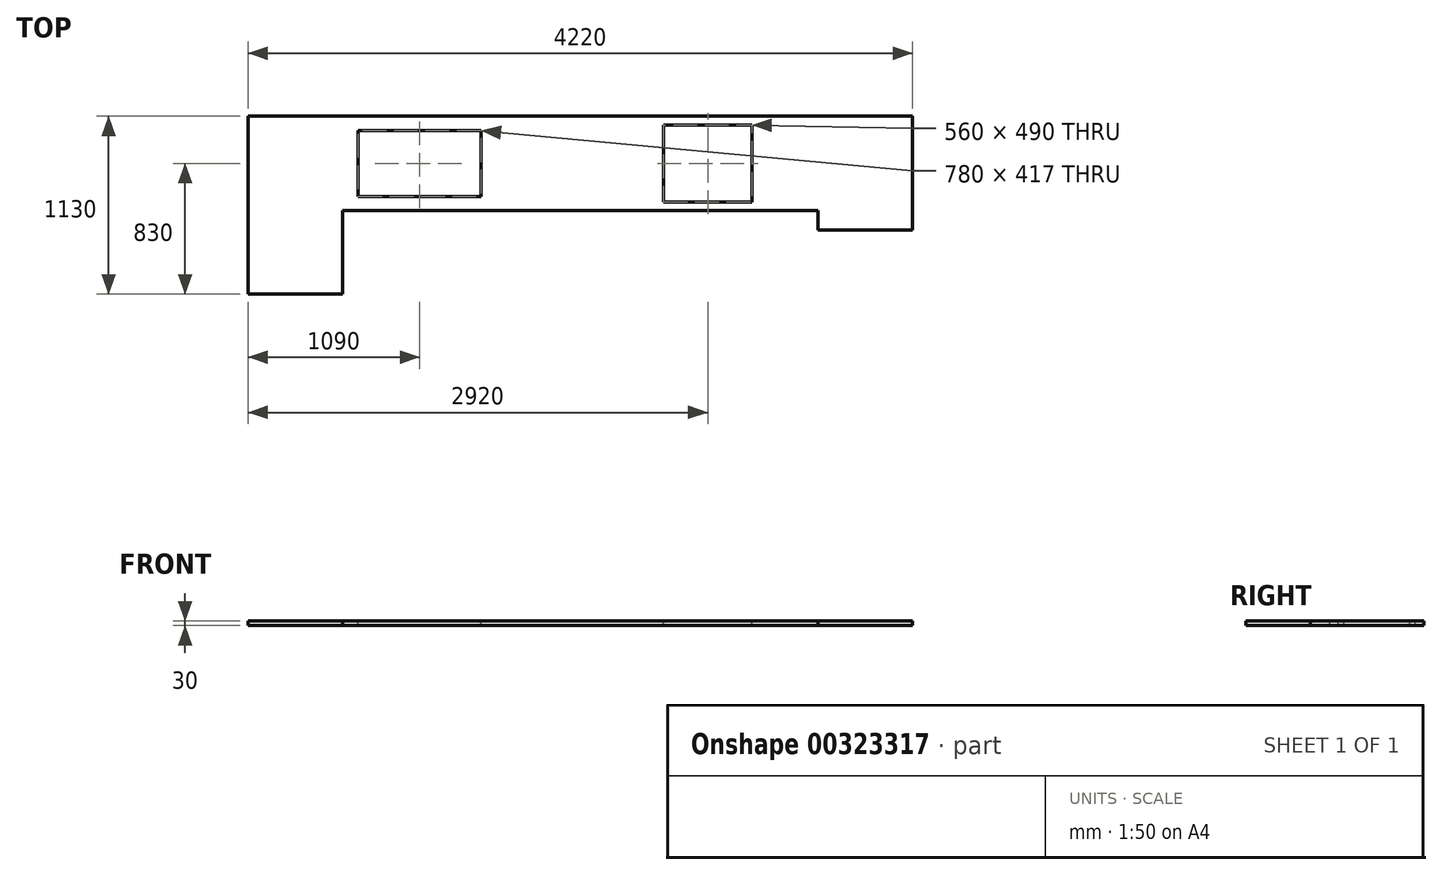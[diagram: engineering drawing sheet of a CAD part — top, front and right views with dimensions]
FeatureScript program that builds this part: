
annotation { "Feature Type Name" : "Feature", "Feature Type Description" : "" }
export const myFeature = defineFeature(function(context is Context, id is Id, definition is map)
    precondition{}
    {
        {
            var Q0;
            Q0=qCreatedBy(makeId("Top.planeOp"),FACE);
            var sketch = newSketch(context, id + "F0", { "sketchPlane" : qUnion([Q0])});
            skLineSegment(sketch, "E0", {"start": v(0, 0) * mm, "end": v(0, 1760) * mm});
            skLineSegment(sketch, "E1", {"start": v(0, 1760) * mm, "end": v(4220, 1760) * mm});
            skLineSegment(sketch, "E2", {"start": v(4220, 1760) * mm, "end": v(4220, 0) * mm});
            skLineSegment(sketch, "E3.0", {"start": v(600, 1160) * mm, "end": v(3620, 1160) * mm});
            skLineSegment(sketch, "E4.0", {"start": v(600, 0) * mm, "end": v(600, 1160) * mm});
            skLineSegment(sketch, "E5.0", {"start": v(3620, 1160) * mm, "end": v(3620, 0) * mm});
            skLineSegment(sketch, "E6", {"start": v(600, 0) * mm, "end": v(0, 0) * mm});
            skLineSegment(sketch, "E7", {"start": v(3620, 0) * mm, "end": v(4220, 0) * mm});
            skSolve(sketch);
        }
        {
            var Q0;
            Q0=qSketchRegion(id+"F0",true);
            extrude(context, id + "F1", {"entities" : qUnion([Q0]), "depth" : 30 * mm});
        }
        {
            var Q0;
            Q0=makeQuery(id+"F1.opExtrude","CAP_FACE",FACE,{"disambiguationData":[OSD([sQuery(id+"F0.wireOp",EDGE,"E0"),sQuery(id+"F0.wireOp",EDGE,"E1"),sQuery(id+"F0.wireOp",EDGE,"E2"),sQuery(id+"F0.wireOp",EDGE,"E3.0"),sQuery(id+"F0.wireOp",EDGE,"E4.0"),sQuery(id+"F0.wireOp",EDGE,"E5.0"),sQuery(id+"F0.wireOp",EDGE,"E6"),sQuery(id+"F0.wireOp",EDGE,"E7")])],"isStart":false});
            var sketch = newSketch(context, id + "F2", { "sketchPlane" : qUnion([Q0])});
            skLineSegment(sketch, "E8.bottom", {"start": v(700, 1251.5) * mm, "end": v(1480, 1251.5) * mm});
            skLineSegment(sketch, "E8.top", {"start": v(700, 1668.5) * mm, "end": v(1480, 1668.5) * mm});
            skLineSegment(sketch, "E8.left", {"start": v(700, 1251.5) * mm, "end": v(700, 1668.5) * mm});
            skLineSegment(sketch, "E8.right", {"start": v(1480, 1251.5) * mm, "end": v(1480, 1668.5) * mm});
            skLineSegment(sketch, "E9", {"start": v(700, 1460) * mm, "end": v(1480, 1460) * mm, "construction": true});
            skSolve(sketch);
        }
        {
            var Q0;
            Q0 = qSketchRegion(id + "F2", true);
            extrude(context, id + "F3", {"entities" : qUnion([Q0]), "operationType" : NewBodyOperationType.REMOVE, "endBound" : BoundingType.UP_TO_NEXT, "oppositeDirection" : true, "depth" : 25 * mm});
        }
        {
            var Q0;
            Q0=makeQuery(id+"F1.opExtrude","CAP_FACE",FACE,{"disambiguationData":[OSD([sQuery(id+"F0.wireOp",EDGE,"E0"),sQuery(id+"F0.wireOp",EDGE,"E1"),sQuery(id+"F0.wireOp",EDGE,"E2"),sQuery(id+"F0.wireOp",EDGE,"E3.0"),sQuery(id+"F0.wireOp",EDGE,"E4.0"),sQuery(id+"F0.wireOp",EDGE,"E5.0"),sQuery(id+"F0.wireOp",EDGE,"E6"),sQuery(id+"F0.wireOp",EDGE,"E7")])],"isStart":false});
            var sketch = newSketch(context, id + "F4", { "sketchPlane" : qUnion([Q0])});
            skLineSegment(sketch, "E10.bottom", {"start": v(2640, 1215) * mm, "end": v(3200, 1215) * mm});
            skLineSegment(sketch, "E10.top", {"start": v(2640, 1705) * mm, "end": v(3200, 1705) * mm});
            skLineSegment(sketch, "E10.left", {"start": v(2640, 1215) * mm, "end": v(2640, 1705) * mm});
            skLineSegment(sketch, "E10.right", {"start": v(3200, 1215) * mm, "end": v(3200, 1705) * mm});
            skSolve(sketch);
        }
        {
            var Q0;
            Q0 = qSketchRegion(id + "F4", true);
            extrude(context, id + "F5", {"entities" : qUnion([Q0]), "operationType" : NewBodyOperationType.REMOVE, "endBound" : BoundingType.UP_TO_NEXT, "oppositeDirection" : true, "depth" : 25 * mm});
        }
        {
            var Q0;
            Q0=makeQuery(id+"F1.opExtrude","CAP_FACE",FACE,{"disambiguationData":[OSD([sQuery(id+"F0.wireOp",EDGE,"E0"),sQuery(id+"F0.wireOp",EDGE,"E1"),sQuery(id+"F0.wireOp",EDGE,"E2"),sQuery(id+"F0.wireOp",EDGE,"E3.0"),sQuery(id+"F0.wireOp",EDGE,"E4.0"),sQuery(id+"F0.wireOp",EDGE,"E5.0"),sQuery(id+"F0.wireOp",EDGE,"E6"),sQuery(id+"F0.wireOp",EDGE,"E7")])],"isStart":false});
            var sketch = newSketch(context, id + "F6", { "sketchPlane" : qUnion([Q0])});
            skLineSegment(sketch, "E11.bottom", {"start": v(0, 0) * mm, "end": v(600, 0) * mm});
            skLineSegment(sketch, "E11.top", {"start": v(0, 630) * mm, "end": v(600, 630) * mm});
            skLineSegment(sketch, "E11.left", {"start": v(0, 0) * mm, "end": v(0, 630) * mm});
            skLineSegment(sketch, "E11.right", {"start": v(600, 0) * mm, "end": v(600, 630) * mm});
            skSolve(sketch);
        }
        {
            var Q0;
            Q0 = qSketchRegion(id + "F6", true);
            extrude(context, id + "F7", {"entities" : qUnion([Q0]), "operationType" : NewBodyOperationType.REMOVE, "endBound" : BoundingType.UP_TO_NEXT, "oppositeDirection" : true, "depth" : 25 * mm});
        }
        {
            var Q0;
            Q0=makeQuery(id+"F1.opExtrude","CAP_FACE",FACE,{"disambiguationData":[OSD([sQuery(id+"F0.wireOp",EDGE,"E0"),sQuery(id+"F0.wireOp",EDGE,"E1"),sQuery(id+"F0.wireOp",EDGE,"E2"),sQuery(id+"F0.wireOp",EDGE,"E3.0"),sQuery(id+"F0.wireOp",EDGE,"E4.0"),sQuery(id+"F0.wireOp",EDGE,"E5.0"),sQuery(id+"F0.wireOp",EDGE,"E6"),sQuery(id+"F0.wireOp",EDGE,"E7")])],"isStart":false});
            var sketch = newSketch(context, id + "F8", { "sketchPlane" : qUnion([Q0])});
            skLineSegment(sketch, "E12.bottom", {"start": v(3620, 0) * mm, "end": v(4220, 0) * mm});
            skLineSegment(sketch, "E12.top", {"start": v(3620, 1038) * mm, "end": v(4220, 1038) * mm});
            skLineSegment(sketch, "E12.left", {"start": v(3620, 0) * mm, "end": v(3620, 1038) * mm});
            skLineSegment(sketch, "E12.right", {"start": v(4220, 0) * mm, "end": v(4220, 1038) * mm});
            skSolve(sketch);
        }
        {
            var Q0;
            Q0 = qSketchRegion(id + "F8", true);
            extrude(context, id + "F9", {"entities" : qUnion([Q0]), "operationType" : NewBodyOperationType.REMOVE, "endBound" : BoundingType.UP_TO_NEXT, "oppositeDirection" : true, "depth" : 25 * mm, "offsetDistance" : 25 * mm});
        }
    });
